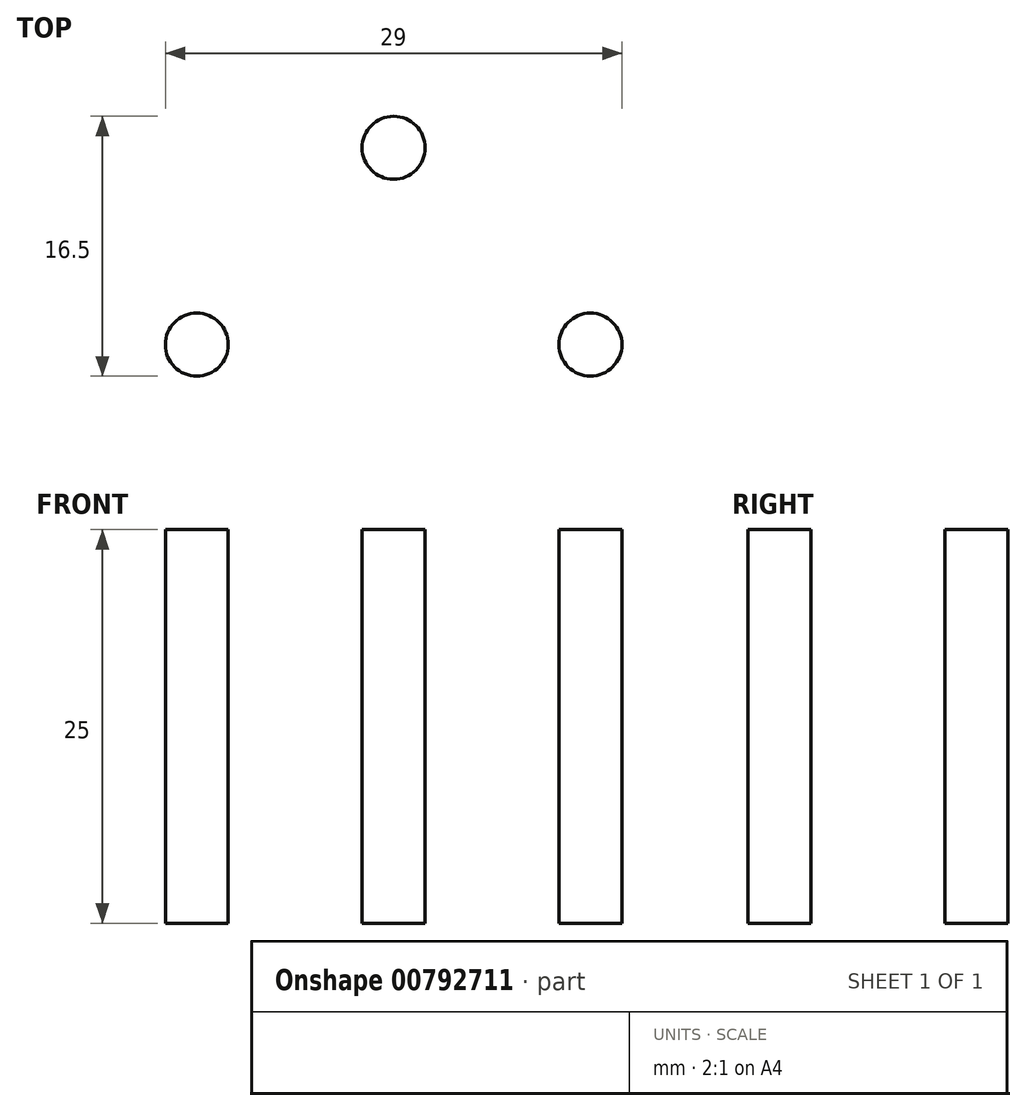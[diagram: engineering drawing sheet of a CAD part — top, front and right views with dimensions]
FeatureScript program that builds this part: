
annotation { "Feature Type Name" : "Feature", "Feature Type Description" : "" }
export const myFeature = defineFeature(function(context is Context, id is Id, definition is map)
    precondition{}
    {
        {
            var Q0;
            Q0=qCreatedBy(makeId("Top.planeOp"),FACE);
            var sketch = newSketch(context, id + "F0", { "sketchPlane" : qUnion([Q0])});
            skCircle(sketch, "E0", {"center": v(-12.5, 0) * mm, "radius": 2 * mm});
            skCircle(sketch, "E1", {"center": v(12.5, 0) * mm, "radius": 2 * mm});
            skCircle(sketch, "E2", {"center": v(0, 12.5) * mm, "radius": 2 * mm});
            skSolve(sketch);
        }
        {
            var Q0;
            Q0=makeQuery(id+"F0.imprint","IMPRINT",FACE,{"disambiguationData":[TD([[makeQuery(id+"F0.imprint","IMPRINT",EDGE,{"derivedFrom":sQuery(id+"F0.wireOp",EDGE,"E0")}),1.0]])]});
            var Q1;
            Q1=makeQuery(id+"F0.imprint","IMPRINT",FACE,{"disambiguationData":[TD([[makeQuery(id+"F0.imprint","IMPRINT",EDGE,{"derivedFrom":sQuery(id+"F0.wireOp",EDGE,"E2")}),1.0]])]});
            var Q2;
            Q2=makeQuery(id+"F0.imprint","IMPRINT",FACE,{"disambiguationData":[TD([[makeQuery(id+"F0.imprint","IMPRINT",EDGE,{"derivedFrom":sQuery(id+"F0.wireOp",EDGE,"E1")}),1.0]])]});
            extrude(context, id + "F1", {"entities" : qUnion([Q0, Q1, Q2]), "depth" : 25 * mm, "offsetDistance" : 25 * mm});
        }
    });
